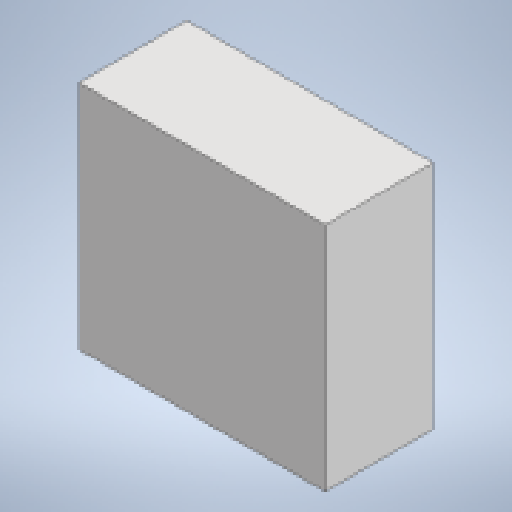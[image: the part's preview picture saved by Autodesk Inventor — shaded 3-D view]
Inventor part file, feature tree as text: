
AUTODESK INVENTOR PART (.ipt)
format: ipt  version: 2025.2 (Build 292293000, 293)  size: 165,888 bytes
history: native  units: mm
features: extrude x4, sketch x4
ambient origin geometry x8: Origin, YZ Plane, XZ Plane, XY Plane, X Axis, Y Axis, Z Axis, Center Point
bodies: Solid1 (feature_tree)
feature tree (8):
  extrude  "Extrusion1"  Depth=101.6mm
  extrude  "Extrusion2"  Depth=76.2mm
  extrude  "Extrusion3"  Depth=50.8mm
  extrude  "Extrusion4"  Depth=5.0mm TaperAngle=0.0deg
  sketch  "Sketch1"  dims[d0=95.25mm d1=101.6mm]
  sketch  "Sketch2"  dims[d2=44.45mm d3=0.0mm d4=76.2mm]
  sketch  "Sketch3"  dims[d5=50.8mm d6=8.0mm]
  sketch  "Sketch4"  dims[d7=15.0mm d8=5.0mm d9=0.0mm d10=12.192mm d11=25.0mm d12=1.27mm d13=0.0mm d14=25.0mm d15=9.128125mm d16=15.24mm d17=0.0mm]
